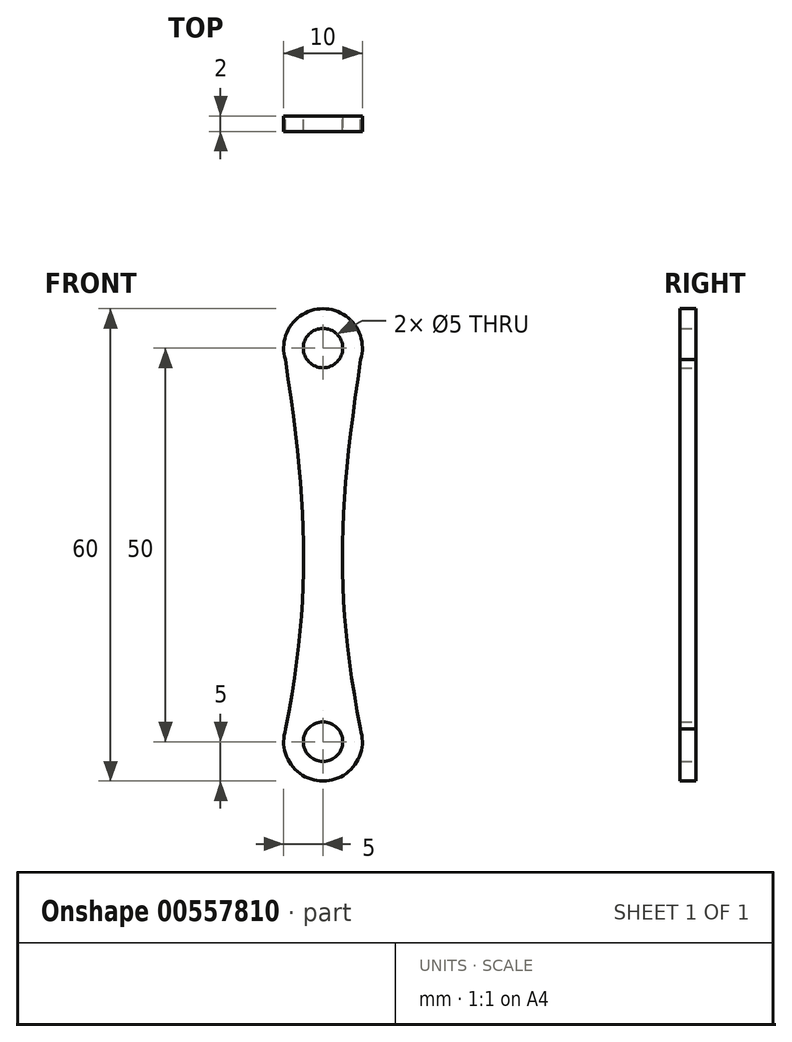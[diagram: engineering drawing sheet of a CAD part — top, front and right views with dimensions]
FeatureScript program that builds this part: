
annotation { "Feature Type Name" : "Feature", "Feature Type Description" : "" }
export const myFeature = defineFeature(function(context is Context, id is Id, definition is map)
    precondition{}
    {
        {
            var Q0;
            Q0=qCreatedBy(makeId("Front.planeOp"),FACE);
            var sketch = newSketch(context, id + "F0", { "sketchPlane" : qUnion([Q0])});
            skCircle(sketch, "E0", {"center": v(0, 0) * mm, "radius": 2.5 * mm});
            skCircle(sketch, "E1", {"center": v(0, 0) * mm, "radius": 5 * mm});
            skCircle(sketch, "E2", {"center": v(0, -50) * mm, "radius": 2.5 * mm});
            skCircle(sketch, "E3", {"center": v(0, -50) * mm, "radius": 5 * mm});
            skFitSpline(sketch, "E4", {"points": [v(5, 0) * mm, v(5, -49.75) * mm], "startDerivative": vector(-9.48, -63.12) * mm, "endDerivative": vector(10.9, -56.62) * mm});
            skLineSegment(sketch, "E5", {"start": v(0, 18.94) * mm, "end": v(0, -62.45) * mm, "construction": true});
            skFitSpline(sketch, "E6.MirrorCS", {"points": [v(-5, 0) * mm, v(-5, -49.75) * mm], "startDerivative": vector(9.48, -63.12) * mm, "endDerivative": vector(-10.9, -56.62) * mm});
            skSolve(sketch);
        }
        {
            var Q0;
            Q0 = qSketchRegion(id + "F0", true);
            extrude(context, id + "F1", {"entities" : qUnion([Q0]), "depth" : 2 * mm, "offsetDistance" : 25 * mm});
        }
    });
